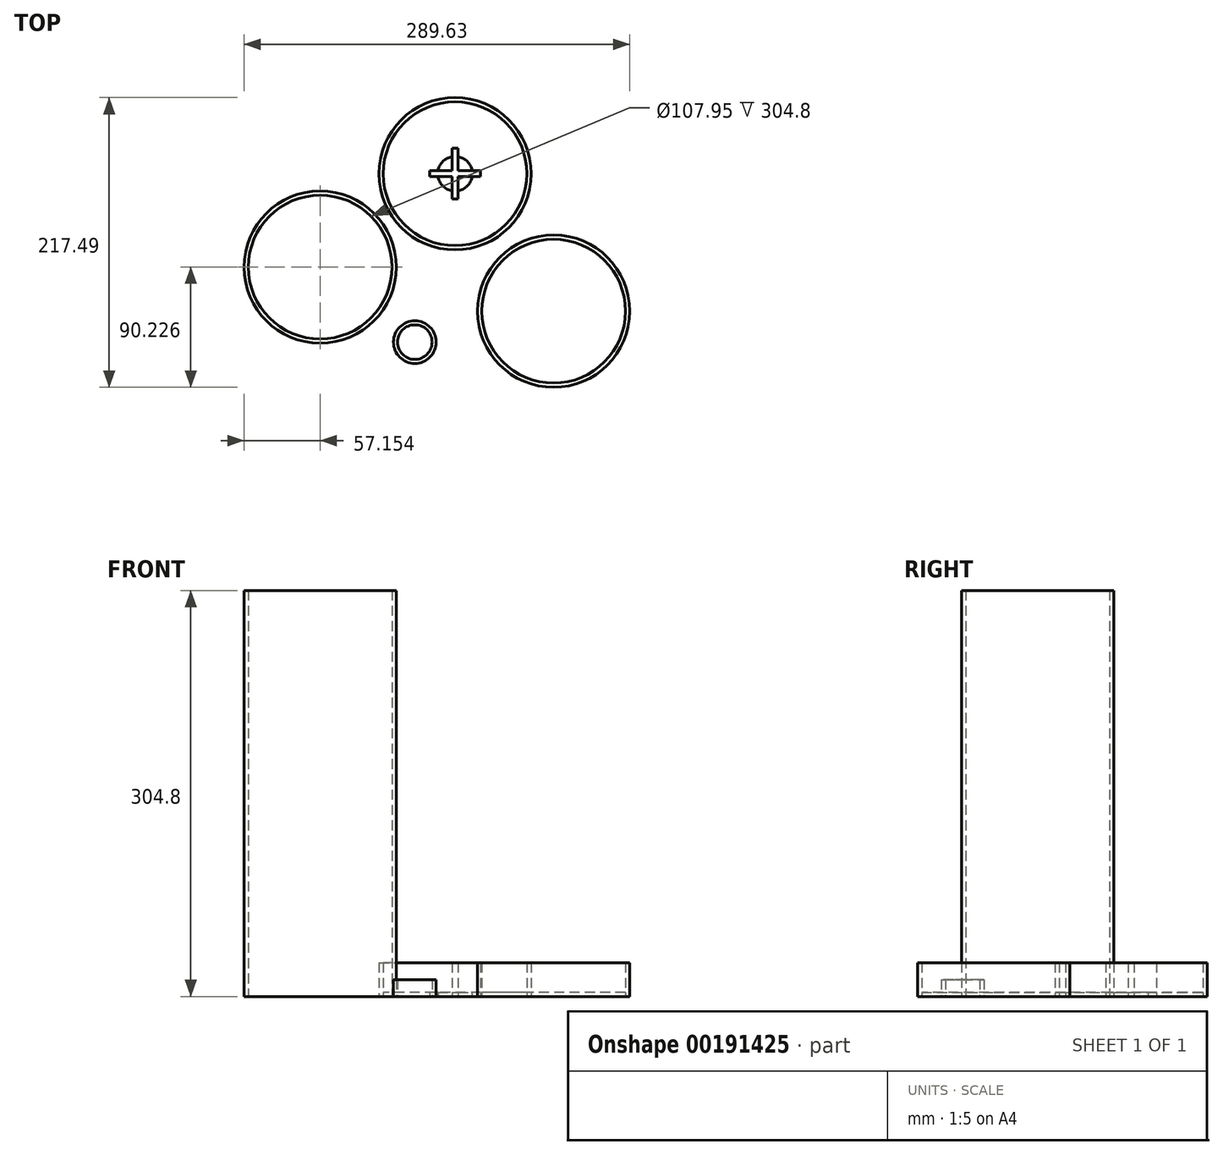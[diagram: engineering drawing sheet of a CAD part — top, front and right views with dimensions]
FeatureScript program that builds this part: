
annotation { "Feature Type Name" : "Feature", "Feature Type Description" : "" }
export const myFeature = defineFeature(function(context is Context, id is Id, definition is map)
    precondition{}
    {
        {
            var Q0;
            Q0=qCreatedBy(makeId("Top.planeOp"),FACE);
            var sketch = newSketch(context, id + "F0", { "sketchPlane" : qUnion([Q0])});
            skCircle(sketch, "E0", {"center": v(0, 0) * mm, "radius": 57.15 * mm});
            skCircle(sketch, "E1", {"center": v(0, 0) * mm, "radius": 53.98 * mm});
            skCircle(sketch, "E2", {"center": v(-175.33, 33.08) * mm, "radius": 57.15 * mm});
            skCircle(sketch, "E3", {"center": v(-175.33, 33.08) * mm, "radius": 53.98 * mm});
            skCircle(sketch, "E4", {"center": v(-74.03, 103.19) * mm, "radius": 53.98 * mm});
            skCircle(sketch, "E5", {"center": v(-74.03, 103.19) * mm, "radius": 57.15 * mm});
            skCircle(sketch, "E6", {"center": v(-74.03, 103.19) * mm, "radius": 13 * mm});
            skLineSegment(sketch, "E7.bottom", {"start": v(-76.26, 122.24) * mm, "end": v(-71.81, 122.24) * mm});
            skLineSegment(sketch, "E7.top", {"start": v(-76.26, 84.14) * mm, "end": v(-71.81, 84.14) * mm});
            skLineSegment(sketch, "E7.left", {"start": v(-76.26, 122.24) * mm, "end": v(-76.26, 84.14) * mm});
            skLineSegment(sketch, "E7.right", {"start": v(-71.81, 122.24) * mm, "end": v(-71.81, 84.14) * mm});
            skLineSegment(sketch, "E8.bottom", {"start": v(-54.98, 100.97) * mm, "end": v(-93.08, 100.97) * mm});
            skLineSegment(sketch, "E8.top", {"start": v(-54.98, 105.41) * mm, "end": v(-93.08, 105.41) * mm});
            skLineSegment(sketch, "E8.left", {"start": v(-54.98, 100.97) * mm, "end": v(-54.98, 105.41) * mm});
            skLineSegment(sketch, "E8.right", {"start": v(-93.08, 100.97) * mm, "end": v(-93.08, 105.41) * mm});
            skSolve(sketch);
        }
        {
            var Q0;
            Q0=makeQuery(id+"F0.imprint","IMPRINT",FACE,{"disambiguationData":[TD([[makeQuery(id+"F0.imprint","IMPRINT",EDGE,{"derivedFrom":sQuery(id+"F0.wireOp",EDGE,"E4")}),1.0]])]});
            var Q1;
            Q1=makeQuery(id+"F0.imprint","IMPRINT",FACE,{"disambiguationData":[TD([[makeQuery(id+"F0.imprint","IMPRINT",EDGE,{"derivedFrom":sQuery(id+"F0.wireOp",EDGE,"E1")}),1.0]])]});
            extrude(context, id + "F1", {"entities" : qUnion([Q0, Q1]), "depth" : 3.17 * mm});
        }
        {
            var Q0;
            {var subQ0=sQuery(id+"F0.wireOp",EDGE,"E7.left");var subQ1=sQuery(id+"F0.wireOp",EDGE,"E6");var subQ2=makeQuery(id+"F0.imprint","INTERSECT",VERTEX,{"disambiguationData":[OD(1.0)],"derivedFrom":[subQ1,subQ0]});Q0=makeQuery(id+"F0.imprint","IMPRINT",FACE,{"disambiguationData":[TD([[makeQuery(id+"F0.imprint","IMPRINT",EDGE,{"disambiguationData":[TD([[subQ2,-1.0]])],"derivedFrom":subQ1}),1.0]])]});}
            var Q1;
            {var subQ5=sQuery(id+"F0.wireOp",EDGE,"E7.top");Q1=makeQuery(id+"F0.imprint","IMPRINT",FACE,{"disambiguationData":[TD([[makeQuery(id+"F0.imprint","IMPRINT",EDGE,{"derivedFrom":subQ5}),1.0]])]});}
            var Q2;
            {var subQ0=sQuery(id+"F0.wireOp",EDGE,"E7.right");var subQ1=sQuery(id+"F0.wireOp",EDGE,"E6");var subQ2=makeQuery(id+"F0.imprint","INTERSECT",VERTEX,{"disambiguationData":[OD(0.0)],"derivedFrom":[subQ1,subQ0]});Q2=makeQuery(id+"F0.imprint","IMPRINT",FACE,{"disambiguationData":[TD([[makeQuery(id+"F0.imprint","IMPRINT",EDGE,{"disambiguationData":[TD([[subQ2,-1.0]])],"derivedFrom":subQ1}),1.0]])]});}
            var Q3;
            {var subQ5=sQuery(id+"F0.wireOp",EDGE,"E7.bottom");Q3=makeQuery(id+"F0.imprint","IMPRINT",FACE,{"disambiguationData":[TD([[makeQuery(id+"F0.imprint","IMPRINT",EDGE,{"derivedFrom":subQ5}),-1.0]])]});}
            var Q4;
            {var subQ0=sQuery(id+"F0.wireOp",EDGE,"E8.top");var subQ1=sQuery(id+"F0.wireOp",EDGE,"E6");var subQ2=makeQuery(id+"F0.imprint","INTERSECT",VERTEX,{"disambiguationData":[OD(0.0)],"derivedFrom":[subQ1,subQ0]});Q4=makeQuery(id+"F0.imprint","IMPRINT",FACE,{"disambiguationData":[TD([[makeQuery(id+"F0.imprint","IMPRINT",EDGE,{"disambiguationData":[TD([[subQ2,1.0]])],"derivedFrom":subQ1}),1.0]])]});}
            var Q5;
            {var subQ5=sQuery(id+"F0.wireOp",EDGE,"E8.left");Q5=makeQuery(id+"F0.imprint","IMPRINT",FACE,{"disambiguationData":[TD([[makeQuery(id+"F0.imprint","IMPRINT",EDGE,{"derivedFrom":subQ5}),1.0]])]});}
            var Q6;
            {var subQ5=sQuery(id+"F0.wireOp",EDGE,"E8.right");Q6=makeQuery(id+"F0.imprint","IMPRINT",FACE,{"disambiguationData":[TD([[makeQuery(id+"F0.imprint","IMPRINT",EDGE,{"derivedFrom":subQ5}),-1.0]])]});}
            var Q7;
            {var subQ0=sQuery(id+"F0.wireOp",EDGE,"E8.top");var subQ1=sQuery(id+"F0.wireOp",EDGE,"E6");var subQ2=makeQuery(id+"F0.imprint","INTERSECT",VERTEX,{"disambiguationData":[OD(1.0)],"derivedFrom":[subQ1,subQ0]});Q7=makeQuery(id+"F0.imprint","IMPRINT",FACE,{"disambiguationData":[TD([[makeQuery(id+"F0.imprint","IMPRINT",EDGE,{"disambiguationData":[TD([[subQ2,-1.0]])],"derivedFrom":subQ1}),1.0]])]});}
            var Q8;
            {var subQ0=sQuery(id+"F0.wireOp",EDGE,"E8.top");var subQ1=sQuery(id+"F0.wireOp",EDGE,"E7.left");var subQ2=makeQuery(id+"F0.imprint","INTERSECT",VERTEX,{"derivedFrom":[subQ1,subQ0]});Q8=makeQuery(id+"F0.imprint","IMPRINT",FACE,{"disambiguationData":[TD([[makeQuery(id+"F0.imprint","IMPRINT",EDGE,{"disambiguationData":[TD([[subQ2,-1.0]])],"derivedFrom":subQ1}),1.0]])]});}
            var Q9;
            Q9=makeQuery(id+"F0.imprint","IMPRINT",FACE,{"disambiguationData":[TD([[makeQuery(id+"F0.imprint","IMPRINT",EDGE,{"derivedFrom":sQuery(id+"F0.wireOp",EDGE,"E0")}),1.0]])]});
            var Q10;
            Q10=makeQuery(id+"F0.imprint","IMPRINT",FACE,{"disambiguationData":[TD([[makeQuery(id+"F0.imprint","IMPRINT",EDGE,{"derivedFrom":sQuery(id+"F0.wireOp",EDGE,"E4")}),-1.0]])]});
            extrude(context, id + "F2", {"entities" : qUnion([Q0, Q1, Q2, Q3, Q4, Q5, Q6, Q7, Q8, Q9, Q10]), "depth" : 25.4 * mm});
        }
        {
            var Q0;
            Q0=makeQuery(id+"F0.imprint","IMPRINT",FACE,{"disambiguationData":[TD([[makeQuery(id+"F0.imprint","IMPRINT",EDGE,{"derivedFrom":sQuery(id+"F0.wireOp",EDGE,"E2")}),1.0]])]});
            extrude(context, id + "F3", {"entities" : qUnion([Q0]), "depth" : 304.8 * mm});
        }
        {
            var Q0;
            Q0=qCreatedBy(makeId("Top.planeOp"),FACE);
            var sketch = newSketch(context, id + "F4", { "sketchPlane" : qUnion([Q0])});
            skCircle(sketch, "E9", {"center": v(-104.26, -23.23) * mm, "radius": 13 * mm});
            skCircle(sketch, "E10", {"center": v(-104.26, -23.23) * mm, "radius": 16 * mm});
            skSolve(sketch);
        }
        {
            var Q0;
            Q0=makeQuery(id+"F4.imprint","IMPRINT",FACE,{"disambiguationData":[TD([[makeQuery(id+"F4.imprint","IMPRINT",EDGE,{"derivedFrom":sQuery(id+"F4.wireOp",EDGE,"E9")}),-1.0]])]});
            extrude(context, id + "F5", {"entities" : qUnion([Q0]), "depth" : 12.7 * mm});
        }
    });
